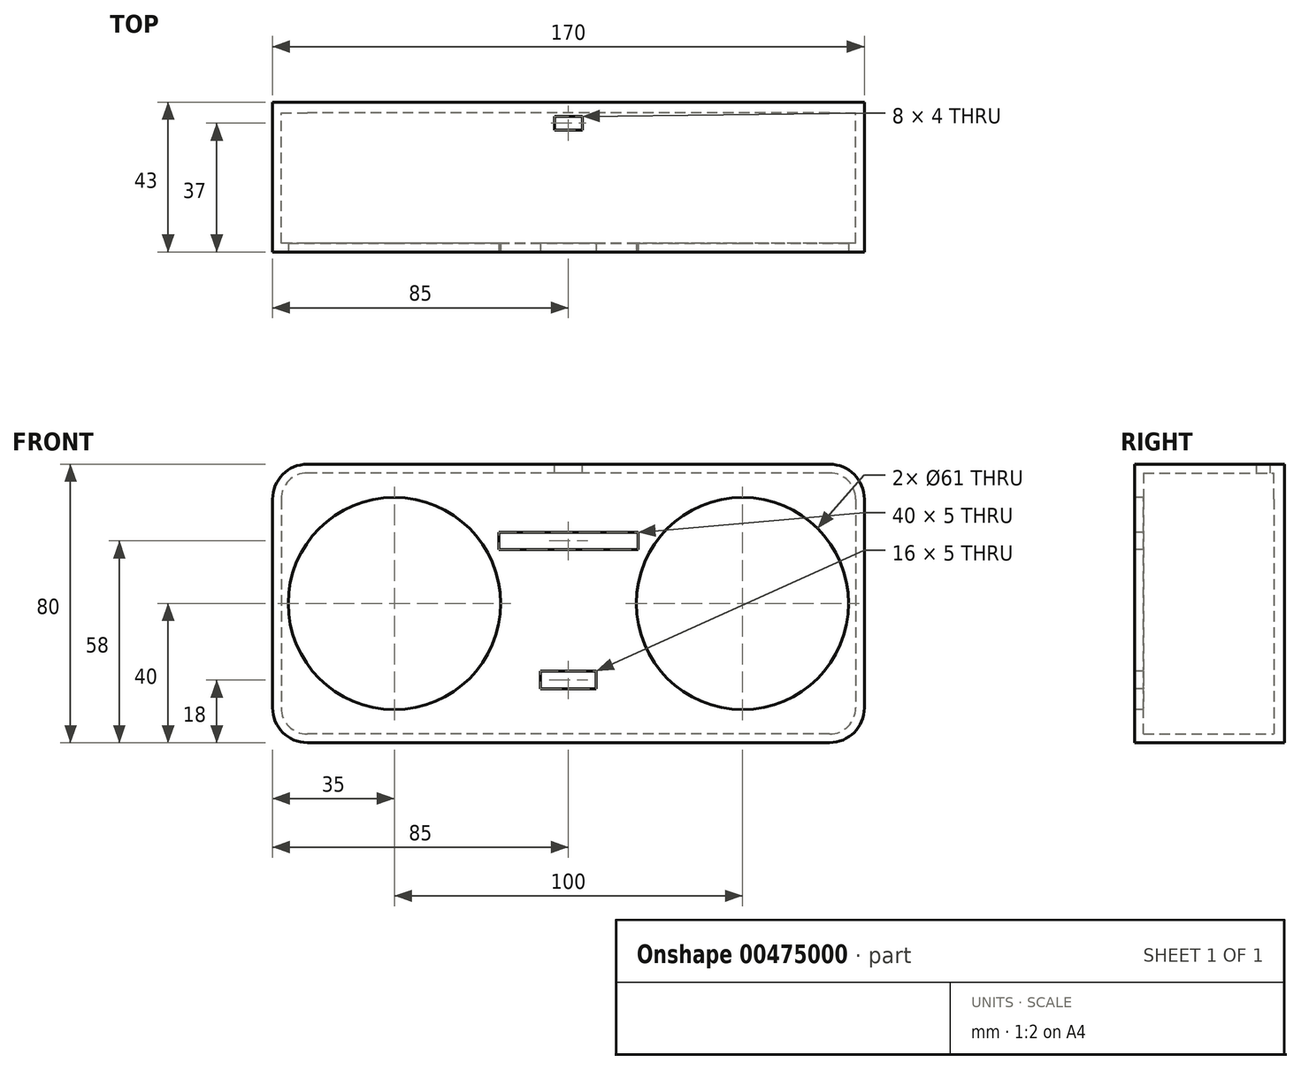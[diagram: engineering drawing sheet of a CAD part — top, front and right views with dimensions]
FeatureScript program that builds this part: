
annotation { "Feature Type Name" : "Feature", "Feature Type Description" : "" }
export const myFeature = defineFeature(function(context is Context, id is Id, definition is map)
    precondition{}
    {
        {
            var Q0;
            Q0=qCreatedBy(makeId("Front.planeOp"),FACE);
            var sketch = newSketch(context, id + "F0", { "sketchPlane" : qUnion([Q0])});
            skLineSegment(sketch, "E0.bottom", {"start": v(75, 40) * mm, "end": v(-75, 40) * mm});
            skLineSegment(sketch, "E0.top", {"start": v(75, -40) * mm, "end": v(-75, -40) * mm});
            skLineSegment(sketch, "E0.left", {"start": v(85, 30) * mm, "end": v(85, -30) * mm});
            skLineSegment(sketch, "E0.right", {"start": v(-85, 30) * mm, "end": v(-85, -30) * mm});
            skPoint(sketch, "E0.middle", {"position": v(0, 0) * mm});
            skPoint(sketch, "E1.visualSharp", {"position": v(-85, 40) * mm});
            skArc(sketch, "E1.filletArc", {"start": v(-75, 40) * mm, "mid": v(-82.07, 37.07) * mm, "end": v(-85, 30) * mm});
            skPoint(sketch, "E2.visualSharp", {"position": v(-85, -40) * mm});
            skArc(sketch, "E2.filletArc", {"start": v(-85, -30) * mm, "mid": v(-82.07, -37.07) * mm, "end": v(-75, -40) * mm});
            skPoint(sketch, "E3.visualSharp", {"position": v(85, -40) * mm});
            skArc(sketch, "E3.filletArc", {"start": v(75, -40) * mm, "mid": v(82.07, -37.07) * mm, "end": v(85, -30) * mm});
            skPoint(sketch, "E4.visualSharp", {"position": v(85, 40) * mm});
            skArc(sketch, "E4.filletArc", {"start": v(85, 30) * mm, "mid": v(82.07, 37.07) * mm, "end": v(75, 40) * mm});
            skSolve(sketch);
        }
        {
            var Q0;
            Q0=makeQuery(id+"F0.imprint","IMPRINT",FACE,{"disambiguationData":[TD([[makeQuery(id+"F0.imprint","IMPRINT",EDGE,{"derivedFrom":sQuery(id+"F0.wireOp",EDGE,"E0.bottom")}),1.0]])]});
            extrude(context, id + "F1", {"entities" : qUnion([Q0]), "depth" : 40 * mm});
        }
        {
            var Q0;
            Q0=makeQuery(id+"F1.opExtrude","CAP_FACE",FACE,{"disambiguationData":[OSD([sQuery(id+"F0.wireOp",EDGE,"E0.bottom"),sQuery(id+"F0.wireOp",EDGE,"E0.top"),sQuery(id+"F0.wireOp",EDGE,"E0.left"),sQuery(id+"F0.wireOp",EDGE,"E0.right"),sQuery(id+"F0.wireOp",EDGE,"E1.filletArc"),sQuery(id+"F0.wireOp",EDGE,"E2.filletArc"),sQuery(id+"F0.wireOp",EDGE,"E3.filletArc"),sQuery(id+"F0.wireOp",EDGE,"E4.filletArc")])],"isStart":true});
            shell(context, id + "F2", {"entities" : qUnion([Q0]), "thickness" : 2.5 * mm});
        }
        {
            var Q0;
            Q0=makeQuery(id+"F1.opExtrude","CAP_FACE",FACE,{"disambiguationData":[OSD([sQuery(id+"F0.wireOp",EDGE,"E0.bottom"),sQuery(id+"F0.wireOp",EDGE,"E0.top"),sQuery(id+"F0.wireOp",EDGE,"E0.left"),sQuery(id+"F0.wireOp",EDGE,"E0.right"),sQuery(id+"F0.wireOp",EDGE,"E1.filletArc"),sQuery(id+"F0.wireOp",EDGE,"E2.filletArc"),sQuery(id+"F0.wireOp",EDGE,"E3.filletArc"),sQuery(id+"F0.wireOp",EDGE,"E4.filletArc")])],"isStart":false});
            var sketch = newSketch(context, id + "F3", { "sketchPlane" : qUnion([Q0])});
            skCircle(sketch, "E5", {"center": v(-50, 0) * mm, "radius": 30.5 * mm});
            skCircle(sketch, "E6", {"center": v(50, 0) * mm, "radius": 30.5 * mm});
            skSolve(sketch);
        }
        {
            var Q0;
            Q0=makeQuery(id+"F3.imprint","IMPRINT",FACE,{"disambiguationData":[TD([[makeQuery(id+"F3.imprint","IMPRINT",EDGE,{"derivedFrom":sQuery(id+"F3.wireOp",EDGE,"E5")}),1.0]])]});
            var Q1;
            Q1=makeQuery(id+"F3.imprint","IMPRINT",FACE,{"disambiguationData":[TD([[makeQuery(id+"F3.imprint","IMPRINT",EDGE,{"derivedFrom":sQuery(id+"F3.wireOp",EDGE,"E6")}),1.0]])]});
            extrude(context, id + "F4", {"entities" : qUnion([Q0, Q1]), "operationType" : NewBodyOperationType.REMOVE, "oppositeDirection" : true, "depth" : 5 * mm});
        }
        {
            var Q0;
            Q0=makeQuery(id+"F1.opExtrude","CAP_FACE",FACE,{"disambiguationData":[OSD([sQuery(id+"F0.wireOp",EDGE,"E0.bottom"),sQuery(id+"F0.wireOp",EDGE,"E0.top"),sQuery(id+"F0.wireOp",EDGE,"E0.left"),sQuery(id+"F0.wireOp",EDGE,"E0.right"),sQuery(id+"F0.wireOp",EDGE,"E1.filletArc"),sQuery(id+"F0.wireOp",EDGE,"E2.filletArc"),sQuery(id+"F0.wireOp",EDGE,"E3.filletArc"),sQuery(id+"F0.wireOp",EDGE,"E4.filletArc")])],"isStart":true});
            var sketch = newSketch(context, id + "F5", { "sketchPlane" : qUnion([Q0])});
            skSolve(sketch);
        }
        {
            var Q0;
            {var subQ3=sQuery(id+"F0.wireOp",EDGE,"E0.bottom");Q0=makeQuery(id+"F5.imprint","IMPRINT",FACE,{"disambiguationData":[TD([[makeQuery(id+"F5.imprint","IMPRINT",EDGE,{"derivedFrom":makeQuery(id+"F2.opShell","OFFSET_EDGE",EDGE,{"disambiguationData":[OSD([subQ3]),TDD([makeQuery(id+"F1.opExtrude","CAP_EDGE",EDGE,{"disambiguationData":[OSD([subQ3])],"isStart":true})])]})}),-1.0]])]});}
            var Q1;
            {var subQ2=sQuery(id+"F0.wireOp",EDGE,"E0.bottom");var subQ3=makeQuery(id+"F1.opExtrude","CAP_EDGE",EDGE,{"disambiguationData":[OSD([subQ2])],"isStart":true});Q1=makeQuery(id+"F5.imprint","IMPRINT",FACE,{"disambiguationData":[TD([[makeQuery(id+"F5.imprint","IMPRINT",EDGE,{"derivedFrom":subQ3}),-1.0]])]});}
            extrude(context, id + "F6", {"entities" : qUnion([Q0, Q1]), "operationType" : NewBodyOperationType.ADD, "depth" : 3 * mm});
        }
        {
            var Q0;
            Q0=makeQuery(id+"F1.opExtrude","CAP_FACE",FACE,{"disambiguationData":[OSD([sQuery(id+"F0.wireOp",EDGE,"E0.bottom"),sQuery(id+"F0.wireOp",EDGE,"E0.top"),sQuery(id+"F0.wireOp",EDGE,"E0.left"),sQuery(id+"F0.wireOp",EDGE,"E0.right"),sQuery(id+"F0.wireOp",EDGE,"E1.filletArc"),sQuery(id+"F0.wireOp",EDGE,"E2.filletArc"),sQuery(id+"F0.wireOp",EDGE,"E3.filletArc"),sQuery(id+"F0.wireOp",EDGE,"E4.filletArc")])],"isStart":false});
            var sketch = newSketch(context, id + "F7", { "sketchPlane" : qUnion([Q0])});
            skLineSegment(sketch, "E7.bottom", {"start": v(-20, 15.5) * mm, "end": v(20, 15.5) * mm});
            skLineSegment(sketch, "E7.top", {"start": v(-20, 20.5) * mm, "end": v(20, 20.5) * mm});
            skLineSegment(sketch, "E7.left", {"start": v(-20, 15.5) * mm, "end": v(-20, 20.5) * mm});
            skLineSegment(sketch, "E7.right", {"start": v(20, 15.5) * mm, "end": v(20, 20.5) * mm});
            skPoint(sketch, "E7.middle", {"position": v(0, 18) * mm});
            skSolve(sketch);
        }
        {
            var Q0;
            Q0 = qSketchRegion(id + "F7", true);
            extrude(context, id + "F8", {"entities" : qUnion([Q0]), "operationType" : NewBodyOperationType.REMOVE, "oppositeDirection" : true, "depth" : 5 * mm});
        }
        {
            var Q0;
            Q0=makeQuery(id+"F1.opExtrude","CAP_FACE",FACE,{"disambiguationData":[OSD([sQuery(id+"F0.wireOp",EDGE,"E0.bottom"),sQuery(id+"F0.wireOp",EDGE,"E0.top"),sQuery(id+"F0.wireOp",EDGE,"E0.left"),sQuery(id+"F0.wireOp",EDGE,"E0.right"),sQuery(id+"F0.wireOp",EDGE,"E1.filletArc"),sQuery(id+"F0.wireOp",EDGE,"E2.filletArc"),sQuery(id+"F0.wireOp",EDGE,"E3.filletArc"),sQuery(id+"F0.wireOp",EDGE,"E4.filletArc")])],"isStart":false});
            var sketch = newSketch(context, id + "F9", { "sketchPlane" : qUnion([Q0])});
            skLineSegment(sketch, "E8.bottom", {"start": v(8, -19.5) * mm, "end": v(-8, -19.5) * mm});
            skLineSegment(sketch, "E8.top", {"start": v(8, -24.5) * mm, "end": v(-8, -24.5) * mm});
            skLineSegment(sketch, "E8.left", {"start": v(8, -19.5) * mm, "end": v(8, -24.5) * mm});
            skLineSegment(sketch, "E8.right", {"start": v(-8, -19.5) * mm, "end": v(-8, -24.5) * mm});
            skPoint(sketch, "E8.middle", {"position": v(0, -22) * mm});
            skSolve(sketch);
        }
        {
            var Q0;
            Q0 = qSketchRegion(id + "F9", true);
            extrude(context, id + "F10", {"entities" : qUnion([Q0]), "operationType" : NewBodyOperationType.REMOVE, "oppositeDirection" : true, "depth" : 5 * mm});
        }
        {
            var Q0;
            {var subQ0=sQuery(id+"F0.wireOp",EDGE,"E0.bottom");Q0=makeQuery(id+"F6.boolean.opBoolean","MERGE",FACE,{"derivedFrom":[makeQuery(id+"F1.opExtrude","SWEPT_FACE",FACE,{"disambiguationData":[OSD([subQ0])]}),makeQuery(id+"F6.opExtrude","SWEPT_FACE",FACE,{"disambiguationData":[OSD([subQ0])]})]});}
            var sketch = newSketch(context, id + "F11", { "sketchPlane" : qUnion([Q0])});
            skLineSegment(sketch, "E9.bottom", {"start": v(4, -5) * mm, "end": v(-4, -5) * mm});
            skLineSegment(sketch, "E9.top", {"start": v(4, -1) * mm, "end": v(-4, -1) * mm});
            skLineSegment(sketch, "E9.left", {"start": v(4, -5) * mm, "end": v(4, -1) * mm});
            skLineSegment(sketch, "E9.right", {"start": v(-4, -5) * mm, "end": v(-4, -1) * mm});
            skPoint(sketch, "E9.middle", {"position": v(0, -3) * mm});
            skSolve(sketch);
        }
        {
            var Q0;
            Q0 = qSketchRegion(id + "F11", true);
            extrude(context, id + "F12", {"entities" : qUnion([Q0]), "operationType" : NewBodyOperationType.REMOVE, "oppositeDirection" : true, "depth" : 2.5 * mm});
        }
    });
